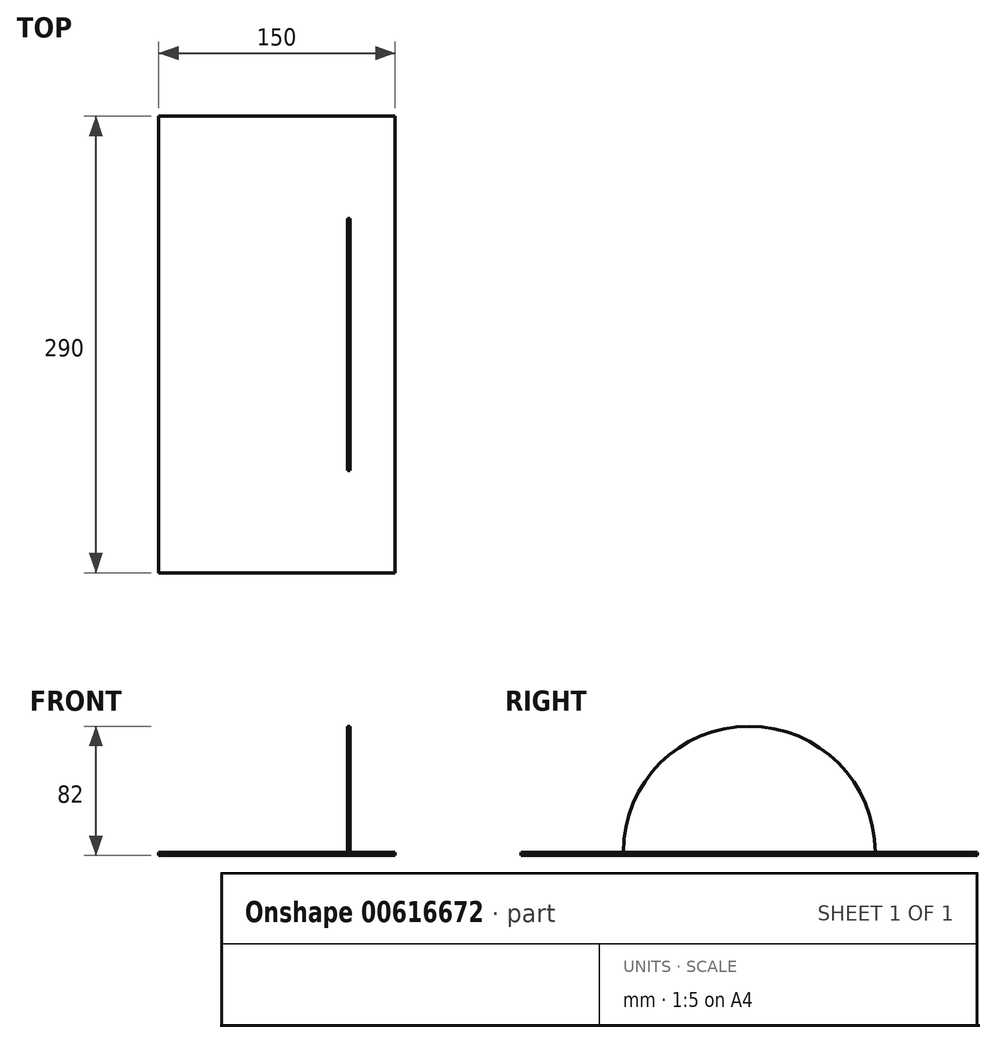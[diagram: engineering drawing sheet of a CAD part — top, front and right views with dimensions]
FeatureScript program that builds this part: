
annotation { "Feature Type Name" : "Feature", "Feature Type Description" : "" }
export const myFeature = defineFeature(function(context is Context, id is Id, definition is map)
    precondition{}
    {
        {
            var Q0;
            Q0=qCreatedBy(makeId("Top.planeOp"),FACE);
            var sketch = newSketch(context, id + "F0", { "sketchPlane" : qUnion([Q0])});
            skLineSegment(sketch, "E0.bottom", {"start": v(0, 0) * mm, "end": v(150, 0) * mm});
            skLineSegment(sketch, "E0.top", {"start": v(0, 290) * mm, "end": v(150, 290) * mm});
            skLineSegment(sketch, "E0.left", {"start": v(0, 0) * mm, "end": v(0, 290) * mm});
            skLineSegment(sketch, "E0.right", {"start": v(150, 0) * mm, "end": v(150, 290) * mm});
            skSolve(sketch);
        }
        {
            var Q0;
            Q0=makeQuery(id+"F0.imprint","IMPRINT",FACE,{"disambiguationData":[TD([[makeQuery(id+"F0.imprint","IMPRINT",EDGE,{"derivedFrom":sQuery(id+"F0.wireOp",EDGE,"E0.bottom")}),1.0]])]});
            extrude(context, id + "F1", {"entities" : qUnion([Q0]), "depth" : 2 * mm, "offsetDistance" : 25 * mm});
        }
        {
            var Q0;
            Q0=makeQuery(id+"F1.opExtrude","CAP_FACE",FACE,{"disambiguationData":[OSD([sQuery(id+"F0.wireOp",EDGE,"E0.bottom"),sQuery(id+"F0.wireOp",EDGE,"E0.top"),sQuery(id+"F0.wireOp",EDGE,"E0.left"),sQuery(id+"F0.wireOp",EDGE,"E0.right")])],"isStart":false});
            var sketch = newSketch(context, id + "F2", { "sketchPlane" : qUnion([Q0])});
            skLineSegment(sketch, "E1.bottom", {"start": v(120, 225) * mm, "end": v(121.5, 225) * mm});
            skLineSegment(sketch, "E1.top", {"start": v(120, 65) * mm, "end": v(121.5, 65) * mm});
            skLineSegment(sketch, "E1.left", {"start": v(120, 225) * mm, "end": v(120, 65) * mm});
            skLineSegment(sketch, "E1.right", {"start": v(121.5, 225) * mm, "end": v(121.5, 65) * mm});
            skLineSegment(sketch, "E2", {"start": v(72.42, 145) * mm, "end": v(37.62, 145) * mm});
            skSolve(sketch);
        }
        {
            var Q0;
            Q0=makeQuery(id+"F2.imprint","IMPRINT",FACE,{"disambiguationData":[TD([[makeQuery(id+"F2.imprint","IMPRINT",EDGE,{"derivedFrom":sQuery(id+"F2.wireOp",EDGE,"E1.bottom")}),-1.0]])]});
            extrude(context, id + "F3", {"entities" : qUnion([Q0]), "operationType" : NewBodyOperationType.ADD, "depth" : 80 * mm, "offsetDistance" : 25 * mm});
        }
        {
            var Q0;
            Q0=makeQuery(id+"F3.opExtrude","SWEPT_FACE",FACE,{"disambiguationData":[OSD([sQuery(id+"F2.wireOp",EDGE,"E1.right")])]});
            var sketch = newSketch(context, id + "F4", { "sketchPlane" : qUnion([Q0])});
            skCircle(sketch, "E3", {"center": v(145, 2) * mm, "radius": 80 * mm});
            skSolve(sketch);
        }
        {
            var Q0;
            {var subQ1=sQuery(id+"F2.wireOp",EDGE,"E1.right");var subQ2=makeQuery(id+"F3.opExtrude","SWEPT_EDGE",EDGE,{"disambiguationData":[OSD([sQuery(id+"F2.wireOp",EDGE,"E1.top"),subQ1])]});Q0=makeQuery(id+"F4.imprint","IMPRINT",FACE,{"disambiguationData":[TD([[makeQuery(id+"F4.imprint","IMPRINT",EDGE,{"derivedFrom":subQ2}),1.0]])]});}
            var Q1;
            {var subQ1=sQuery(id+"F2.wireOp",EDGE,"E1.right");var subQ2=makeQuery(id+"F3.opExtrude","SWEPT_EDGE",EDGE,{"disambiguationData":[OSD([sQuery(id+"F2.wireOp",EDGE,"E1.bottom"),subQ1])]});Q1=makeQuery(id+"F4.imprint","IMPRINT",FACE,{"disambiguationData":[TD([[makeQuery(id+"F4.imprint","IMPRINT",EDGE,{"derivedFrom":subQ2}),-1.0]])]});}
            extrude(context, id + "F5", {"entities" : qUnion([Q0, Q1]), "operationType" : NewBodyOperationType.REMOVE, "oppositeDirection" : true, "depth" : 25 * mm, "offsetDistance" : 25 * mm});
        }
    });
